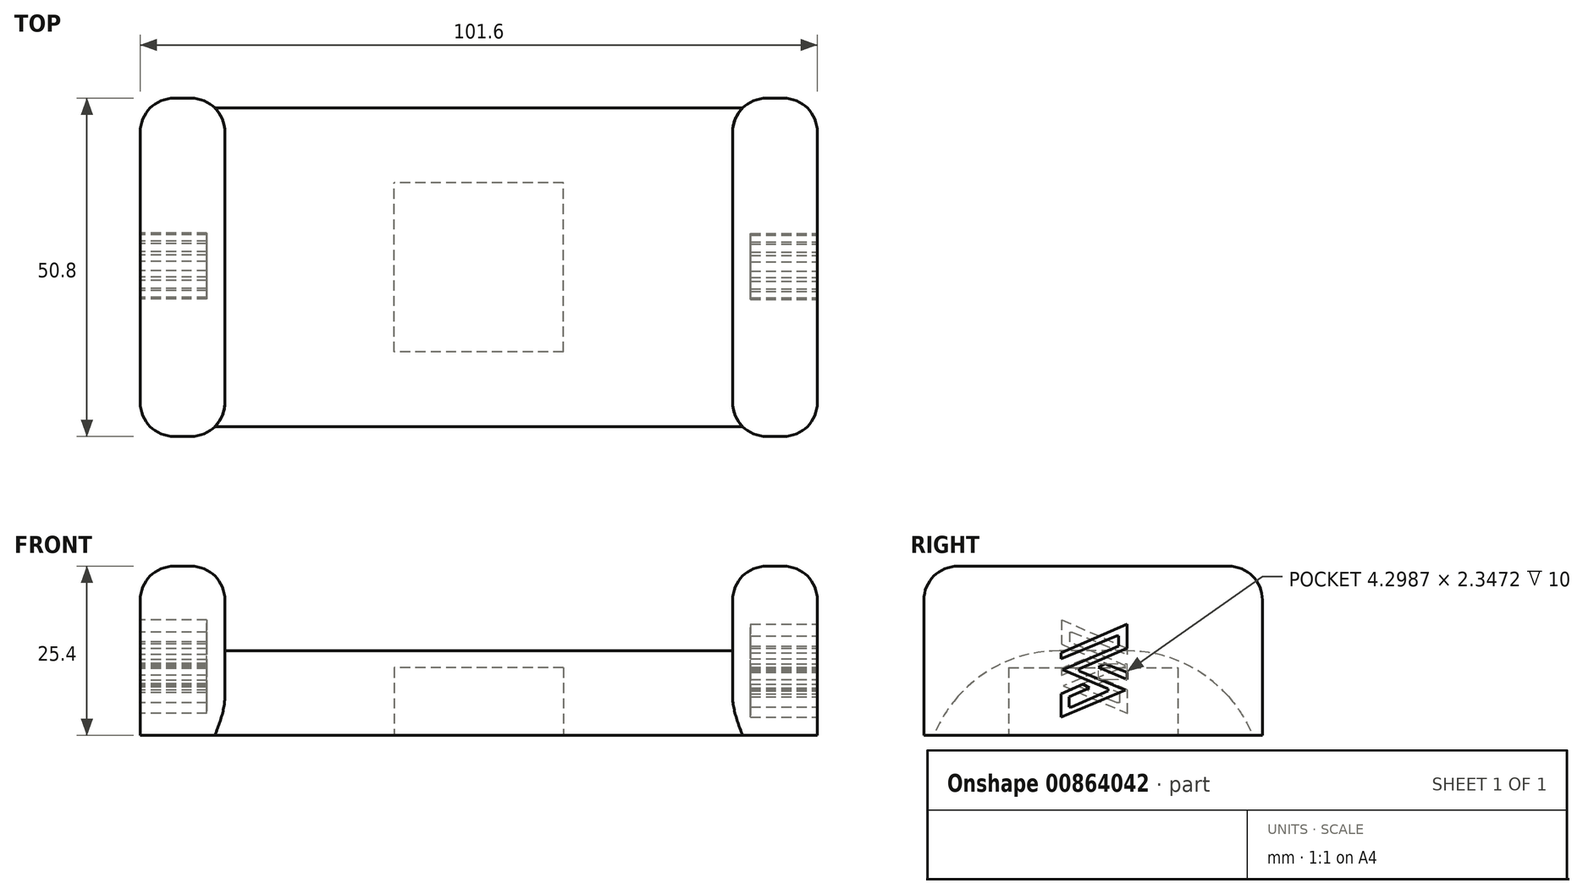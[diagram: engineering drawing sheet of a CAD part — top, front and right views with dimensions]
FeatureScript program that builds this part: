
annotation { "Feature Type Name" : "Feature", "Feature Type Description" : "" }
export const myFeature = defineFeature(function(context is Context, id is Id, definition is map)
    precondition{}
    {
        {
            var Q0;
            Q0=qCreatedBy(makeId("Top.planeOp"),FACE);
            var sketch = newSketch(context, id + "F0", { "sketchPlane" : qUnion([Q0])});
            skLineSegment(sketch, "E0.bottom", {"start": v(50.8, 25.4) * mm, "end": v(-50.8, 25.4) * mm});
            skLineSegment(sketch, "E0.top", {"start": v(50.8, -25.4) * mm, "end": v(-50.8, -25.4) * mm});
            skLineSegment(sketch, "E0.left", {"start": v(50.8, 25.4) * mm, "end": v(50.8, -25.4) * mm});
            skLineSegment(sketch, "E0.right", {"start": v(-50.8, 25.4) * mm, "end": v(-50.8, -25.4) * mm});
            skPoint(sketch, "E0.middle", {"position": v(0, 0) * mm});
            skSolve(sketch);
        }
        {
            var Q0;
            Q0=makeQuery(id+"F0.imprint","IMPRINT",FACE,{"disambiguationData":[TD([[makeQuery(id+"F0.imprint","IMPRINT",EDGE,{"derivedFrom":sQuery(id+"F0.wireOp",EDGE,"E0.bottom")}),1.0]])]});
            extrude(context, id + "F1", {"entities" : qUnion([Q0]), "depth" : 12.7 * mm, "offsetDistance" : 25.4 * mm});
        }
        {
            var Q0;
            Q0=makeQuery(id+"F1.opExtrude","CAP_FACE",FACE,{"disambiguationData":[OSD([sQuery(id+"F0.wireOp",EDGE,"E0.bottom"),sQuery(id+"F0.wireOp",EDGE,"E0.top"),sQuery(id+"F0.wireOp",EDGE,"E0.left"),sQuery(id+"F0.wireOp",EDGE,"E0.right")])],"isStart":false});
            var sketch = newSketch(context, id + "F2", { "sketchPlane" : qUnion([Q0])});
            skLineSegment(sketch, "E1.bottom", {"start": v(-50.8, 25.4) * mm, "end": v(-38.1, 25.4) * mm});
            skLineSegment(sketch, "E1.top", {"start": v(-50.8, -25.4) * mm, "end": v(-38.1, -25.4) * mm});
            skLineSegment(sketch, "E1.left", {"start": v(-50.8, 25.4) * mm, "end": v(-50.8, -25.4) * mm});
            skLineSegment(sketch, "E1.right", {"start": v(-38.1, 25.4) * mm, "end": v(-38.1, -25.4) * mm});
            skSolve(sketch);
        }
        {
            var Q0;
            Q0=makeQuery(id+"F2.imprint","IMPRINT",FACE,{"disambiguationData":[TD([[makeQuery(id+"F2.imprint","IMPRINT",EDGE,{"derivedFrom":sQuery(id+"F2.wireOp",EDGE,"E1.bottom")}),1.0]])]});
            extrude(context, id + "F3", {"entities" : qUnion([Q0]), "operationType" : NewBodyOperationType.ADD, "depth" : 12.7 * mm, "offsetDistance" : 25.4 * mm});
        }
        {
            var Q0;
            Q0=makeQuery(id+"F3.opExtrude","CAP_EDGE",EDGE,{"disambiguationData":[OSD([sQuery(id+"F2.wireOp",EDGE,"E1.right")])],"isStart":false});
            var Q1;
            Q1=makeQuery(id+"F3.opExtrude","CAP_EDGE",EDGE,{"disambiguationData":[OSD([sQuery(id+"F2.wireOp",EDGE,"E1.left")])],"isStart":false});
            var Q2;
            Q2=makeQuery(id+"F3.opExtrude","CAP_EDGE",EDGE,{"disambiguationData":[OSD([sQuery(id+"F2.wireOp",EDGE,"E1.top")])],"isStart":false});
            var Q3;
            Q3=makeQuery(id+"F3.opExtrude","CAP_EDGE",EDGE,{"disambiguationData":[OSD([sQuery(id+"F2.wireOp",EDGE,"E1.bottom")])],"isStart":false});
            fillet(context, id + "F4", {"entities" : qUnion([Q0, Q1, Q2, Q3]), "radius" : 5.08 * mm, "tangentPropagation" : true, "allowEdgeOverflow" : false});
        }
        {
            var Q0;
            Q0=makeQuery(id+"F1.opExtrude","CAP_FACE",FACE,{"disambiguationData":[OSD([sQuery(id+"F0.wireOp",EDGE,"E0.bottom"),sQuery(id+"F0.wireOp",EDGE,"E0.top"),sQuery(id+"F0.wireOp",EDGE,"E0.left"),sQuery(id+"F0.wireOp",EDGE,"E0.right")])],"isStart":true});
            var sketch = newSketch(context, id + "F5", { "sketchPlane" : qUnion([Q0])});
            skLineSegment(sketch, "E2.bottom", {"start": v(12.7, 12.7) * mm, "end": v(-12.7, 12.7) * mm});
            skLineSegment(sketch, "E2.top", {"start": v(12.7, -12.7) * mm, "end": v(-12.7, -12.7) * mm});
            skLineSegment(sketch, "E2.left", {"start": v(12.7, 12.7) * mm, "end": v(12.7, -12.7) * mm});
            skLineSegment(sketch, "E2.right", {"start": v(-12.7, 12.7) * mm, "end": v(-12.7, -12.7) * mm});
            skPoint(sketch, "E2.middle", {"position": v(0, 0) * mm});
            skSolve(sketch);
        }
        {
            var Q0;
            Q0=makeQuery(id+"F1.opExtrude","CAP_FACE",FACE,{"disambiguationData":[OSD([sQuery(id+"F0.wireOp",EDGE,"E0.bottom"),sQuery(id+"F0.wireOp",EDGE,"E0.top"),sQuery(id+"F0.wireOp",EDGE,"E0.left"),sQuery(id+"F0.wireOp",EDGE,"E0.right")])],"isStart":false});
            var sketch = newSketch(context, id + "F6", { "sketchPlane" : qUnion([Q0])});
            skLineSegment(sketch, "E3.bottom", {"start": v(50.8, 25.4) * mm, "end": v(38.1, 25.4) * mm});
            skLineSegment(sketch, "E3.top", {"start": v(50.8, -25.4) * mm, "end": v(38.1, -25.4) * mm});
            skLineSegment(sketch, "E3.left", {"start": v(50.8, 25.4) * mm, "end": v(50.8, -25.4) * mm});
            skLineSegment(sketch, "E3.right", {"start": v(38.1, 25.4) * mm, "end": v(38.1, -25.4) * mm});
            skSolve(sketch);
        }
        {
            var Q0;
            Q0=makeQuery(id+"F6.imprint","IMPRINT",FACE,{"disambiguationData":[TD([[makeQuery(id+"F6.imprint","IMPRINT",EDGE,{"derivedFrom":sQuery(id+"F6.wireOp",EDGE,"E3.bottom")}),1.0]])]});
            extrude(context, id + "F7", {"entities" : qUnion([Q0]), "operationType" : NewBodyOperationType.ADD, "depth" : 12.7 * mm, "offsetDistance" : 25.4 * mm});
        }
        {
            var Q0;
            Q0=makeQuery(id+"F7.opExtrude","CAP_EDGE",EDGE,{"disambiguationData":[OSD([sQuery(id+"F6.wireOp",EDGE,"E3.right")])],"isStart":false});
            var Q1;
            Q1=makeQuery(id+"F7.opExtrude","CAP_EDGE",EDGE,{"disambiguationData":[OSD([sQuery(id+"F6.wireOp",EDGE,"E3.left")])],"isStart":false});
            var Q2;
            Q2=makeQuery(id+"F7.opExtrude","CAP_EDGE",EDGE,{"disambiguationData":[OSD([sQuery(id+"F6.wireOp",EDGE,"E3.top")])],"isStart":false});
            var Q3;
            Q3=makeQuery(id+"F7.opExtrude","CAP_EDGE",EDGE,{"disambiguationData":[OSD([sQuery(id+"F6.wireOp",EDGE,"E3.bottom")])],"isStart":false});
            fillet(context, id + "F8", {"entities" : qUnion([Q0, Q1, Q2, Q3]), "radius" : 5.08 * mm, "tangentPropagation" : true, "allowEdgeOverflow" : false});
        }
        {
            var Q0;
            Q0=makeQuery(id+"F1.opExtrude","CAP_EDGE",EDGE,{"disambiguationData":[OSD([sQuery(id+"F0.wireOp",EDGE,"E0.top")])],"isStart":false});
            var Q1;
            Q1=makeQuery(id+"F1.opExtrude","CAP_EDGE",EDGE,{"disambiguationData":[OSD([sQuery(id+"F0.wireOp",EDGE,"E0.bottom")])],"isStart":false});
            fillet(context, id + "F9", {"entities" : qUnion([Q0, Q1]), "radius" : 20.32 * mm, "tangentPropagation" : true, "allowEdgeOverflow" : false});
        }
        {
            var Q0;
            Q0=makeQuery(id+"F3.opExtrude","SWEPT_EDGE",EDGE,{"disambiguationData":[OSD([sQuery(id+"F0.wireOp",EDGE,"E0.top"),sQuery(id+"F2.wireOp",EDGE,"E1.top"),sQuery(id+"F2.wireOp",EDGE,"E1.right")])]});
            var Q1;
            Q1=makeQuery(id+"F3.opExtrude","SWEPT_EDGE",EDGE,{"disambiguationData":[OSD([sQuery(id+"F0.wireOp",EDGE,"E0.bottom"),sQuery(id+"F2.wireOp",EDGE,"E1.bottom"),sQuery(id+"F2.wireOp",EDGE,"E1.right")])]});
            var Q2;
            Q2=makeQuery(id+"F3.boolean.opBoolean","MERGE",EDGE,{"derivedFrom":[makeQuery(id+"F1.opExtrude","SWEPT_EDGE",EDGE,{"disambiguationData":[OSD([sQuery(id+"F0.wireOp",EDGE,"E0.bottom"),sQuery(id+"F0.wireOp",EDGE,"E0.right")])]}),makeQuery(id+"F3.opExtrude","SWEPT_EDGE",EDGE,{"disambiguationData":[OSD([sQuery(id+"F2.wireOp",EDGE,"E1.bottom"),sQuery(id+"F2.wireOp",EDGE,"E1.left")])]})]});
            var Q3;
            Q3=makeQuery(id+"F3.boolean.opBoolean","MERGE",EDGE,{"derivedFrom":[makeQuery(id+"F1.opExtrude","SWEPT_EDGE",EDGE,{"disambiguationData":[OSD([sQuery(id+"F0.wireOp",EDGE,"E0.top"),sQuery(id+"F0.wireOp",EDGE,"E0.right")])]}),makeQuery(id+"F3.opExtrude","SWEPT_EDGE",EDGE,{"disambiguationData":[OSD([sQuery(id+"F2.wireOp",EDGE,"E1.top"),sQuery(id+"F2.wireOp",EDGE,"E1.left")])]})]});
            var Q4;
            Q4=makeQuery(id+"F7.opExtrude","SWEPT_EDGE",EDGE,{"disambiguationData":[OSD([sQuery(id+"F0.wireOp",EDGE,"E0.top"),sQuery(id+"F6.wireOp",EDGE,"E3.top"),sQuery(id+"F6.wireOp",EDGE,"E3.right")])]});
            var Q5;
            Q5=makeQuery(id+"F7.boolean.opBoolean","MERGE",EDGE,{"derivedFrom":[makeQuery(id+"F1.opExtrude","SWEPT_EDGE",EDGE,{"disambiguationData":[OSD([sQuery(id+"F0.wireOp",EDGE,"E0.top"),sQuery(id+"F0.wireOp",EDGE,"E0.left")])]}),makeQuery(id+"F7.opExtrude","SWEPT_EDGE",EDGE,{"disambiguationData":[OSD([sQuery(id+"F6.wireOp",EDGE,"E3.top"),sQuery(id+"F6.wireOp",EDGE,"E3.left")])]})]});
            var Q6;
            Q6=makeQuery(id+"F7.boolean.opBoolean","MERGE",EDGE,{"derivedFrom":[makeQuery(id+"F1.opExtrude","SWEPT_EDGE",EDGE,{"disambiguationData":[OSD([sQuery(id+"F0.wireOp",EDGE,"E0.bottom"),sQuery(id+"F0.wireOp",EDGE,"E0.left")])]}),makeQuery(id+"F7.opExtrude","SWEPT_EDGE",EDGE,{"disambiguationData":[OSD([sQuery(id+"F6.wireOp",EDGE,"E3.bottom"),sQuery(id+"F6.wireOp",EDGE,"E3.left")])]})]});
            var Q7;
            Q7=makeQuery(id+"F7.opExtrude","SWEPT_EDGE",EDGE,{"disambiguationData":[OSD([sQuery(id+"F0.wireOp",EDGE,"E0.bottom"),sQuery(id+"F6.wireOp",EDGE,"E3.bottom"),sQuery(id+"F6.wireOp",EDGE,"E3.right")])]});
            fillet(context, id + "F10", {"entities" : qUnion([Q0, Q1, Q2, Q3, Q4, Q5, Q6, Q7]), "radius" : 5.08 * mm, "tangentPropagation" : true, "allowEdgeOverflow" : false});
        }
        {
            var Q0;
            Q0=makeQuery(id+"F5.imprint","IMPRINT",FACE,{"disambiguationData":[TD([[makeQuery(id+"F5.imprint","IMPRINT",EDGE,{"derivedFrom":sQuery(id+"F5.wireOp",EDGE,"E2.bottom")}),1.0]])]});
            extrude(context, id + "F11", {"entities" : qUnion([Q0]), "operationType" : NewBodyOperationType.REMOVE, "oppositeDirection" : true, "depth" : 10.16 * mm, "offsetDistance" : 25.4 * mm});
        }
        {
            var Q0;
            Q0=makeQuery(id+"F7.boolean.opBoolean","MERGE",FACE,{"derivedFrom":[makeQuery(id+"F1.opExtrude","SWEPT_FACE",FACE,{"disambiguationData":[OSD([sQuery(id+"F0.wireOp",EDGE,"E0.left")])]}),makeQuery(id+"F7.opExtrude","SWEPT_FACE",FACE,{"disambiguationData":[OSD([sQuery(id+"F6.wireOp",EDGE,"E3.left")])]})]});
            var sketch = newSketch(context, id + "F12", { "sketchPlane" : qUnion([Q0])});
            skLineSegment(sketch, "E4", {"start": v(-4.84, 12.4) * mm, "end": v(5.1, 16.73) * mm});
            skLineSegment(sketch, "E5", {"start": v(5.1, 16.73) * mm, "end": v(5.1, 13.1) * mm});
            skLineSegment(sketch, "E6", {"start": v(5.1, 13.1) * mm, "end": v(-2.07, 10) * mm});
            skLineSegment(sketch, "E7", {"start": v(-2.07, 10) * mm, "end": v(-2.07, 9.67) * mm});
            skLineSegment(sketch, "E8", {"start": v(-2.07, 9.67) * mm, "end": v(4.8, 6.82) * mm});
            skLineSegment(sketch, "E9", {"start": v(4.8, 6.82) * mm, "end": v(-4.83, 2.72) * mm});
            skLineSegment(sketch, "E10", {"start": v(-4.83, 2.72) * mm, "end": v(-4.83, 6.21) * mm});
            skLineSegment(sketch, "E11", {"start": v(-4.83, 6.21) * mm, "end": v(-1.54, 7.68) * mm});
            skLineSegment(sketch, "E12", {"start": v(-1.54, 7.68) * mm, "end": v(-0.55, 7.14) * mm});
            skLineSegment(sketch, "E13", {"start": v(-0.55, 7.14) * mm, "end": v(-3.6, 5.8) * mm});
            skLineSegment(sketch, "E14", {"start": v(-3.6, 5.8) * mm, "end": v(-3.6, 4.28) * mm});
            skLineSegment(sketch, "E15", {"start": v(-3.6, 4.28) * mm, "end": v(-3.26, 4.28) * mm});
            skLineSegment(sketch, "E16", {"start": v(-3.26, 4.28) * mm, "end": v(2.26, 6.64) * mm});
            skLineSegment(sketch, "E17", {"start": v(2.26, 6.64) * mm, "end": v(2.26, 7) * mm});
            skLineSegment(sketch, "E18", {"start": v(2.26, 7) * mm, "end": v(-4.59, 9.84) * mm});
            skLineSegment(sketch, "E19", {"start": v(-4.59, 9.84) * mm, "end": v(3.8, 13.43) * mm});
            skLineSegment(sketch, "E20", {"start": v(3.8, 13.43) * mm, "end": v(3.8, 14.92) * mm});
            skPoint(sketch, "E20.endSnap0", {"position": v(5.1, 14.92) * mm});
            skLineSegment(sketch, "E21", {"start": v(3.8, 14.92) * mm, "end": v(3.47, 14.92) * mm});
            skLineSegment(sketch, "E22", {"start": v(3.47, 14.92) * mm, "end": v(-4.83, 11.5) * mm});
            skLineSegment(sketch, "E23", {"start": v(-4.83, 11.5) * mm, "end": v(-4.84, 12.4) * mm});
            skLineSegment(sketch, "E24", {"start": v(0.8, 10.22) * mm, "end": v(1.78, 10.77) * mm});
            skLineSegment(sketch, "E25", {"start": v(1.78, 10.77) * mm, "end": v(5.1, 9.46) * mm});
            skLineSegment(sketch, "E26", {"start": v(5.1, 9.46) * mm, "end": v(5.1, 8.42) * mm});
            skLineSegment(sketch, "E27", {"start": v(5.1, 8.42) * mm, "end": v(0.8, 10.22) * mm});
            skSolve(sketch);
        }
        {
            var Q0;
            Q0=makeQuery(id+"F12.imprint","IMPRINT",FACE,{"disambiguationData":[TD([[makeQuery(id+"F12.imprint","IMPRINT",EDGE,{"derivedFrom":sQuery(id+"F12.wireOp",EDGE,"E4")}),-1.0]])]});
            var Q1;
            Q1=makeQuery(id+"F12.imprint","IMPRINT",FACE,{"disambiguationData":[TD([[makeQuery(id+"F12.imprint","IMPRINT",EDGE,{"derivedFrom":sQuery(id+"F12.wireOp",EDGE,"E24")}),-1.0]])]});
            extrude(context, id + "F13", {"entities" : qUnion([Q0, Q1]), "operationType" : NewBodyOperationType.REMOVE, "oppositeDirection" : true, "depth" : 10 * mm, "offsetDistance" : 25 * mm});
        }
        {
            var Q0;
            Q0=makeQuery(id+"F3.boolean.opBoolean","MERGE",FACE,{"derivedFrom":[makeQuery(id+"F1.opExtrude","SWEPT_FACE",FACE,{"disambiguationData":[OSD([sQuery(id+"F0.wireOp",EDGE,"E0.right")])]}),makeQuery(id+"F3.opExtrude","SWEPT_FACE",FACE,{"disambiguationData":[OSD([sQuery(id+"F2.wireOp",EDGE,"E1.left")])]})]});
            var sketch = newSketch(context, id + "F14", { "sketchPlane" : qUnion([Q0])});
            skLineSegment(sketch, "E28", {"start": v(-5.15, 13) * mm, "end": v(4.78, 17.34) * mm});
            skLineSegment(sketch, "E29", {"start": v(4.78, 17.34) * mm, "end": v(4.78, 13.7) * mm});
            skLineSegment(sketch, "E30", {"start": v(4.78, 13.7) * mm, "end": v(-2.38, 10.6) * mm});
            skLineSegment(sketch, "E31", {"start": v(-2.38, 10.6) * mm, "end": v(-2.38, 10.28) * mm});
            skLineSegment(sketch, "E32", {"start": v(-2.38, 10.28) * mm, "end": v(4.49, 7.42) * mm});
            skLineSegment(sketch, "E33", {"start": v(4.49, 7.42) * mm, "end": v(-5.15, 3.32) * mm});
            skLineSegment(sketch, "E34", {"start": v(-5.15, 3.32) * mm, "end": v(-5.15, 6.82) * mm});
            skLineSegment(sketch, "E35", {"start": v(-5.15, 6.82) * mm, "end": v(-1.85, 8.29) * mm});
            skLineSegment(sketch, "E36", {"start": v(-1.85, 8.29) * mm, "end": v(-0.86, 7.74) * mm});
            skLineSegment(sketch, "E37", {"start": v(-0.86, 7.74) * mm, "end": v(-3.92, 6.4) * mm});
            skLineSegment(sketch, "E38", {"start": v(-3.92, 6.4) * mm, "end": v(-3.92, 4.89) * mm});
            skLineSegment(sketch, "E39", {"start": v(-3.92, 4.89) * mm, "end": v(-3.57, 4.89) * mm});
            skLineSegment(sketch, "E40", {"start": v(-3.57, 4.89) * mm, "end": v(1.94, 7.25) * mm});
            skLineSegment(sketch, "E41", {"start": v(1.94, 7.25) * mm, "end": v(1.94, 7.6) * mm});
            skLineSegment(sketch, "E42", {"start": v(1.94, 7.6) * mm, "end": v(-4.9, 10.44) * mm});
            skLineSegment(sketch, "E43", {"start": v(-4.9, 10.44) * mm, "end": v(3.48, 14.03) * mm});
            skLineSegment(sketch, "E44", {"start": v(3.48, 14.03) * mm, "end": v(3.48, 15.52) * mm});
            skPoint(sketch, "E44.endSnap0", {"position": v(4.78, 15.52) * mm});
            skLineSegment(sketch, "E45", {"start": v(3.48, 15.52) * mm, "end": v(3.15, 15.52) * mm});
            skLineSegment(sketch, "E46", {"start": v(3.15, 15.52) * mm, "end": v(-5.15, 12.1) * mm});
            skLineSegment(sketch, "E47", {"start": v(-5.15, 12.1) * mm, "end": v(-5.15, 13) * mm});
            skLineSegment(sketch, "E48", {"start": v(0.49, 10.83) * mm, "end": v(1.47, 11.37) * mm});
            skLineSegment(sketch, "E49", {"start": v(1.47, 11.37) * mm, "end": v(4.78, 10.06) * mm});
            skLineSegment(sketch, "E50", {"start": v(4.78, 10.06) * mm, "end": v(4.78, 9.02) * mm});
            skLineSegment(sketch, "E51", {"start": v(4.78, 9.02) * mm, "end": v(0.49, 10.83) * mm});
            skSolve(sketch);
        }
        {
            var Q0;
            Q0=makeQuery(id+"F14.imprint","IMPRINT",FACE,{"disambiguationData":[TD([[makeQuery(id+"F14.imprint","IMPRINT",EDGE,{"derivedFrom":sQuery(id+"F14.wireOp",EDGE,"E28")}),-1.0]])]});
            var Q1;
            Q1=makeQuery(id+"F14.imprint","IMPRINT",FACE,{"disambiguationData":[TD([[makeQuery(id+"F14.imprint","IMPRINT",EDGE,{"derivedFrom":sQuery(id+"F14.wireOp",EDGE,"E48")}),-1.0]])]});
            extrude(context, id + "F15", {"entities" : qUnion([Q0, Q1]), "operationType" : NewBodyOperationType.REMOVE, "oppositeDirection" : true, "depth" : 10 * mm, "offsetDistance" : 25 * mm});
        }
    });
